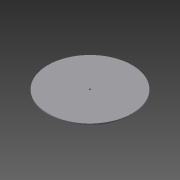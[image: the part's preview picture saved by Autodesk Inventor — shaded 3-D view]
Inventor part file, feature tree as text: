
AUTODESK INVENTOR PART (.ipt)
format: ipt  version: 2013 (Build 170138000, 138)  size: 77,824 bytes
history: native  units: in
note: dims shown in document units (in); Inventor stores cm internally (conversion verified against a paired STEP export)
features: extrude x1, sketch x1
ambient origin geometry x8: Origin, YZ Plane, XZ Plane, XY Plane, X Axis, Y Axis, Z Axis, Center Point
bodies: Solid1 (feature_tree)
feature tree (2):
  extrude  "Extrusion1"  Depth=0.75in TaperAngle=0.0deg
  sketch  "Sketch1"  dims[d0=48.0in d2=0.75in d3=0.0in d5=1.0in d6=0.205in d7=23.5in d8=1.5748in d10=360.0deg]
